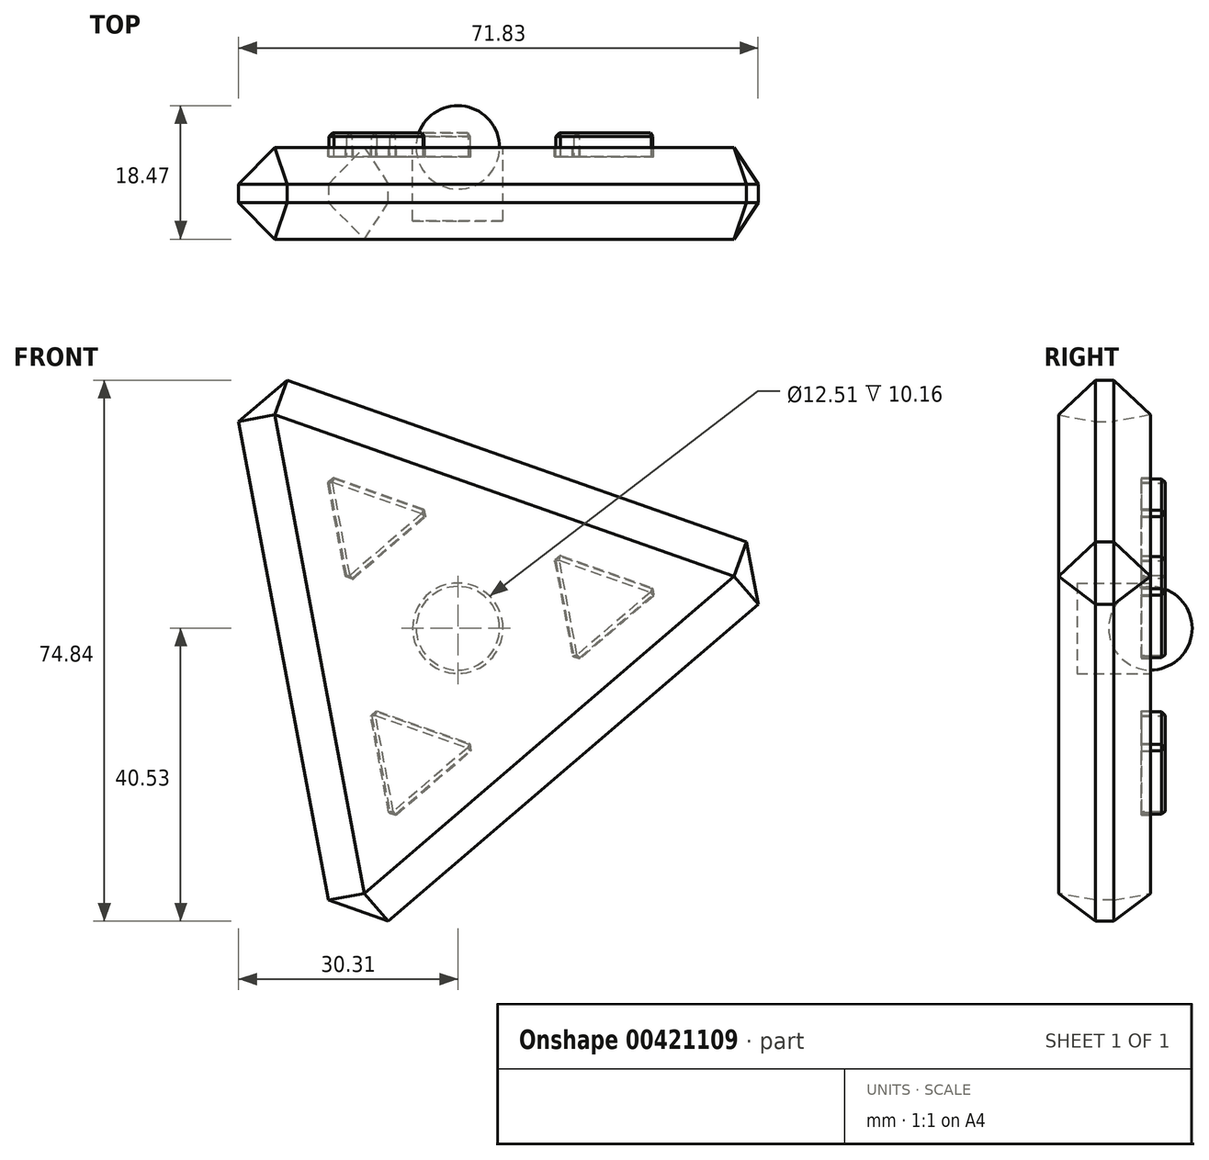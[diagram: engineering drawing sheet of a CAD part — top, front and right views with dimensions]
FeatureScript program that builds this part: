
annotation { "Feature Type Name" : "Feature", "Feature Type Description" : "" }
export const myFeature = defineFeature(function(context is Context, id is Id, definition is map)
    precondition{}
    {
        {
            var Q0;
            Q0=qCreatedBy(makeId("Front.planeOp"),FACE);
            var sketch = newSketch(context, id + "F0", { "sketchPlane" : qUnion([Q0])});
            skCircle(sketch, "E0.cCircle", {"center": v(0, 0) * mm, "radius": 49.04 * mm, "construction": true});
            skLineSegment(sketch, "E0.0", {"start": v(-16.28, -46.26) * mm, "end": v(-31.93, 37.23) * mm});
            skLineSegment(sketch, "E0.1", {"start": v(-31.93, 37.23) * mm, "end": v(48.2, 9.03) * mm});
            skLineSegment(sketch, "E0.2", {"start": v(48.2, 9.03) * mm, "end": v(-16.28, -46.26) * mm});
            skSolve(sketch);
        }
        {
            var Q0;
            Q0=makeQuery(id+"F0.imprint","IMPRINT",FACE,{"disambiguationData":[TD([[makeQuery(id+"F0.imprint","IMPRINT",EDGE,{"derivedFrom":sQuery(id+"F0.wireOp",EDGE,"E0.0")}),-1.0]])]});
            extrude(context, id + "F1", {"entities" : qUnion([Q0]), "depth" : 12.7 * mm});
        }
        {
            var Q0;
            Q0=makeQuery(id+"F1.opExtrude","CAP_FACE",FACE,{"disambiguationData":[OSD([sQuery(id+"F0.wireOp",EDGE,"E0.0"),sQuery(id+"F0.wireOp",EDGE,"E0.1"),sQuery(id+"F0.wireOp",EDGE,"E0.2")])],"isStart":true});
            var Q1;
            Q1=makeQuery(id+"F1.opExtrude","SWEPT_EDGE",EDGE,{"disambiguationData":[OSD([sQuery(id+"F0.wireOp",EDGE,"E0.1"),sQuery(id+"F0.wireOp",EDGE,"E0.2")])]});
            var Q2;
            Q2=makeQuery(id+"F1.opExtrude","SWEPT_EDGE",EDGE,{"disambiguationData":[OSD([sQuery(id+"F0.wireOp",EDGE,"E0.0"),sQuery(id+"F0.wireOp",EDGE,"E0.1")])]});
            var Q3;
            Q3=makeQuery(id+"F1.opExtrude","SWEPT_EDGE",EDGE,{"disambiguationData":[OSD([sQuery(id+"F0.wireOp",EDGE,"E0.0"),sQuery(id+"F0.wireOp",EDGE,"E0.2")])]});
            var Q4;
            Q4=makeQuery(id+"F1.opExtrude","CAP_FACE",FACE,{"disambiguationData":[OSD([sQuery(id+"F0.wireOp",EDGE,"E0.0"),sQuery(id+"F0.wireOp",EDGE,"E0.1"),sQuery(id+"F0.wireOp",EDGE,"E0.2")])],"isStart":false});
            chamfer(context, id + "F2", {"entities" : qUnion([Q0, Q1, Q2, Q3, Q4]), "width" : 5.08 * mm, "tangentPropagation" : true});
        }
        {
            var Q0;
            Q0=makeQuery(id+"F1.opExtrude","CAP_FACE",FACE,{"disambiguationData":[OSD([sQuery(id+"F0.wireOp",EDGE,"E0.0"),sQuery(id+"F0.wireOp",EDGE,"E0.1"),sQuery(id+"F0.wireOp",EDGE,"E0.2")])],"isStart":true});
            var sketch = newSketch(context, id + "F3", { "sketchPlane" : qUnion([Q0])});
            skCircle(sketch, "E1", {"center": v(0, 0) * mm, "radius": 6.26 * mm});
            skSolve(sketch);
        }
        {
            var Q0;
            Q0 = qSketchRegion(id + "F3", true);
            extrude(context, id + "F4", {"entities" : qUnion([Q0]), "operationType" : NewBodyOperationType.REMOVE, "oppositeDirection" : true, "depth" : 10.16 * mm});
        }
        {
            var Q0;
            Q0=makeQuery(id+"F1.opExtrude","CAP_FACE",FACE,{"disambiguationData":[OSD([sQuery(id+"F0.wireOp",EDGE,"E0.0"),sQuery(id+"F0.wireOp",EDGE,"E0.1"),sQuery(id+"F0.wireOp",EDGE,"E0.2")])],"isStart":true});
            var sketch = newSketch(context, id + "F5", { "sketchPlane" : qUnion([Q0])});
            skPoint(sketch, "E2", {"position": v(12.4, 14.46) * mm});
            skPoint(sketch, "E3", {"position": v(6.32, -17.97) * mm});
            skPoint(sketch, "E4", {"position": v(-19.05, 3.57) * mm});
            skCircle(sketch, "E5.cCircle", {"center": v(12.4, 14.46) * mm, "radius": 8.57 * mm, "construction": true});
            skLineSegment(sketch, "E5.0", {"start": v(17.98, 20.97) * mm, "end": v(15.25, 6.37) * mm});
            skLineSegment(sketch, "E5.1", {"start": v(15.25, 6.37) * mm, "end": v(3.98, 16.04) * mm});
            skLineSegment(sketch, "E5.2", {"start": v(3.98, 16.04) * mm, "end": v(17.98, 20.97) * mm});
            skCircle(sketch, "E6.cCircle", {"center": v(6.32, -17.97) * mm, "radius": 8.8 * mm, "construction": true});
            skLineSegment(sketch, "E6.0", {"start": v(9.24, -26.27) * mm, "end": v(-2.33, -16.35) * mm});
            skLineSegment(sketch, "E6.1", {"start": v(-2.33, -16.35) * mm, "end": v(12.05, -11.29) * mm});
            skLineSegment(sketch, "E6.2", {"start": v(12.05, -11.29) * mm, "end": v(9.24, -26.27) * mm});
            skCircle(sketch, "E7.cCircle", {"center": v(-19.05, 3.57) * mm, "radius": 8.7 * mm, "construction": true});
            skLineSegment(sketch, "E7.0", {"start": v(-27.6, 5.17) * mm, "end": v(-13.38, 10.18) * mm});
            skLineSegment(sketch, "E7.1", {"start": v(-13.38, 10.18) * mm, "end": v(-16.16, -4.64) * mm});
            skLineSegment(sketch, "E7.2", {"start": v(-16.16, -4.64) * mm, "end": v(-27.6, 5.17) * mm});
            skSolve(sketch);
        }
        {
            var Q0;
            Q0 = qSketchRegion(id + "F5", true);
            extrude(context, id + "F6", {"entities" : qUnion([Q0]), "operationType" : NewBodyOperationType.ADD, "depth" : 2.03 * mm});
        }
        {
            var Q0;
            Q0=makeQuery(id+"F6.opExtrude","CAP_FACE",FACE,{"disambiguationData":[OSD([sQuery(id+"F5.wireOp",EDGE,"E7.0"),sQuery(id+"F5.wireOp",EDGE,"E7.1"),sQuery(id+"F5.wireOp",EDGE,"E7.2")])],"isStart":false});
            var Q1;
            Q1=makeQuery(id+"F6.opExtrude","CAP_FACE",FACE,{"disambiguationData":[OSD([sQuery(id+"F5.wireOp",EDGE,"E5.0"),sQuery(id+"F5.wireOp",EDGE,"E5.1"),sQuery(id+"F5.wireOp",EDGE,"E5.2")])],"isStart":false});
            var Q2;
            Q2=makeQuery(id+"F6.opExtrude","CAP_FACE",FACE,{"disambiguationData":[OSD([sQuery(id+"F5.wireOp",EDGE,"E6.0"),sQuery(id+"F5.wireOp",EDGE,"E6.1"),sQuery(id+"F5.wireOp",EDGE,"E6.2")])],"isStart":false});
            var Q3;
            Q3=makeQuery(id+"F6.opExtrude","SWEPT_EDGE",EDGE,{"disambiguationData":[OSD([sQuery(id+"F5.wireOp",EDGE,"E7.1"),sQuery(id+"F5.wireOp",EDGE,"E7.2")])]});
            var Q4;
            Q4=makeQuery(id+"F6.opExtrude","SWEPT_EDGE",EDGE,{"disambiguationData":[OSD([sQuery(id+"F5.wireOp",EDGE,"E7.0"),sQuery(id+"F5.wireOp",EDGE,"E7.2")])]});
            var Q5;
            Q5=makeQuery(id+"F6.opExtrude","SWEPT_EDGE",EDGE,{"disambiguationData":[OSD([sQuery(id+"F5.wireOp",EDGE,"E7.0"),sQuery(id+"F5.wireOp",EDGE,"E7.1")])]});
            var Q6;
            Q6=makeQuery(id+"F6.opExtrude","SWEPT_EDGE",EDGE,{"disambiguationData":[OSD([sQuery(id+"F5.wireOp",EDGE,"E5.1"),sQuery(id+"F5.wireOp",EDGE,"E5.2")])]});
            var Q7;
            Q7=makeQuery(id+"F6.opExtrude","SWEPT_EDGE",EDGE,{"disambiguationData":[OSD([sQuery(id+"F5.wireOp",EDGE,"E5.0"),sQuery(id+"F5.wireOp",EDGE,"E5.2")])]});
            var Q8;
            Q8=makeQuery(id+"F6.opExtrude","SWEPT_EDGE",EDGE,{"disambiguationData":[OSD([sQuery(id+"F5.wireOp",EDGE,"E5.0"),sQuery(id+"F5.wireOp",EDGE,"E5.1")])]});
            var Q9;
            Q9=makeQuery(id+"F6.opExtrude","SWEPT_EDGE",EDGE,{"disambiguationData":[OSD([sQuery(id+"F5.wireOp",EDGE,"E6.0"),sQuery(id+"F5.wireOp",EDGE,"E6.2")])]});
            var Q10;
            Q10=makeQuery(id+"F6.opExtrude","SWEPT_EDGE",EDGE,{"disambiguationData":[OSD([sQuery(id+"F5.wireOp",EDGE,"E6.1"),sQuery(id+"F5.wireOp",EDGE,"E6.2")])]});
            var Q11;
            Q11=makeQuery(id+"F6.opExtrude","SWEPT_EDGE",EDGE,{"disambiguationData":[OSD([sQuery(id+"F5.wireOp",EDGE,"E6.0"),sQuery(id+"F5.wireOp",EDGE,"E6.1")])]});
            chamfer(context, id + "F7", {"entities" : qUnion([Q0, Q1, Q2, Q3, Q4, Q5, Q6, Q7, Q8, Q9, Q10, Q11]), "width" : 0.5 * mm, "tangentPropagation" : true});
        }
        {
            var Q0;
            Q0=makeQuery(id+"F1.opExtrude","CAP_FACE",FACE,{"disambiguationData":[OSD([sQuery(id+"F0.wireOp",EDGE,"E0.0"),sQuery(id+"F0.wireOp",EDGE,"E0.1"),sQuery(id+"F0.wireOp",EDGE,"E0.2")])],"isStart":true});
            var sketch = newSketch(context, id + "F8", { "sketchPlane" : qUnion([Q0])});
            skLineSegment(sketch, "E8", {"start": v(4.65, 16.36) * mm, "end": v(4.5, 15.5) * mm});
            skLineSegment(sketch, "E9", {"start": v(4.5, 15.5) * mm, "end": v(4.5, 15.4) * mm});
            skLineSegment(sketch, "E10", {"start": v(14.58, 6.8) * mm, "end": v(15.46, 7.1) * mm});
            skLineSegment(sketch, "E11", {"start": v(14.58, 6.8) * mm, "end": v(14.48, 6.83) * mm});
            skLineSegment(sketch, "E12", {"start": v(14.48, 6.83) * mm, "end": v(4.5, 15.4) * mm});
            skLineSegment(sketch, "E13", {"start": v(17.15, 20.82) * mm, "end": v(17.96, 20.17) * mm});
            skLineSegment(sketch, "E14", {"start": v(17.15, 20.82) * mm, "end": v(17.09, 20.82) * mm});
            skLineSegment(sketch, "E15", {"start": v(17.09, 20.82) * mm, "end": v(4.8, 16.5) * mm});
            skLineSegment(sketch, "E16", {"start": v(4.65, 16.36) * mm, "end": v(4.8, 16.5) * mm});
            skLineSegment(sketch, "E17", {"start": v(17.96, 20.1) * mm, "end": v(17.96, 20.17) * mm});
            skLineSegment(sketch, "E18", {"start": v(15.55, 7.21) * mm, "end": v(15.46, 7.1) * mm});
            skLineSegment(sketch, "E19", {"start": v(15.55, 7.21) * mm, "end": v(17.96, 20.1) * mm});
            skLineSegment(sketch, "E20", {"start": v(4.8, 16.33) * mm, "end": v(4.64, 15.47) * mm});
            skLineSegment(sketch, "E21", {"start": v(4.64, 15.47) * mm, "end": v(14.58, 6.95) * mm});
            skLineSegment(sketch, "E22", {"start": v(14.58, 6.95) * mm, "end": v(15.4, 7.24) * mm});
            skLineSegment(sketch, "E23", {"start": v(15.4, 7.24) * mm, "end": v(17.82, 20.1) * mm});
            skLineSegment(sketch, "E24", {"start": v(17.82, 20.1) * mm, "end": v(17.15, 20.68) * mm});
            skLineSegment(sketch, "E25", {"start": v(17.15, 20.68) * mm, "end": v(4.8, 16.33) * mm});
            skSolve(sketch);
        }
        {
            var Q0;
            Q0 = qSketchRegion(id + "F8", true);
            extrude(context, id + "F9", {"entities" : qUnion([Q0]), "operationType" : NewBodyOperationType.REMOVE, "oppositeDirection" : true, "depth" : 1.27 * mm});
        }
        {
            var Q0;
            Q0=makeQuery(id+"F1.opExtrude","CAP_FACE",FACE,{"disambiguationData":[OSD([sQuery(id+"F0.wireOp",EDGE,"E0.0"),sQuery(id+"F0.wireOp",EDGE,"E0.1"),sQuery(id+"F0.wireOp",EDGE,"E0.2")])],"isStart":true});
            var sketch = newSketch(context, id + "F10", { "sketchPlane" : qUnion([Q0])});
            skLineSegment(sketch, "E26", {"start": v(-1.66, -16.03) * mm, "end": v(-1.8, -16.92) * mm});
            skLineSegment(sketch, "E27", {"start": v(-1.66, -16.03) * mm, "end": v(-1.55, -15.9) * mm});
            skLineSegment(sketch, "E28", {"start": v(-1.76, -17.03) * mm, "end": v(-1.8, -16.92) * mm});
            skLineSegment(sketch, "E29", {"start": v(12.04, -12.18) * mm, "end": v(12, -12.04) * mm});
            skLineSegment(sketch, "E30", {"start": v(11.32, -11.47) * mm, "end": v(11.22, -11.44) * mm});
            skLineSegment(sketch, "E31", {"start": v(11.32, -11.47) * mm, "end": v(12, -12.04) * mm});
            skLineSegment(sketch, "E32", {"start": v(11.22, -11.44) * mm, "end": v(-1.55, -15.9) * mm});
            skLineSegment(sketch, "E33", {"start": v(8.49, -25.8) * mm, "end": v(8.58, -25.86) * mm});
            skLineSegment(sketch, "E34", {"start": v(9.56, -25.44) * mm, "end": v(9.46, -25.56) * mm});
            skLineSegment(sketch, "E35", {"start": v(9.46, -25.56) * mm, "end": v(8.58, -25.86) * mm});
            skLineSegment(sketch, "E36", {"start": v(8.49, -25.8) * mm, "end": v(-1.76, -17.03) * mm});
            skLineSegment(sketch, "E37", {"start": v(9.56, -25.44) * mm, "end": v(12.04, -12.18) * mm});
            skLineSegment(sketch, "E38", {"start": v(11.22, -11.58) * mm, "end": v(11.9, -12.15) * mm});
            skLineSegment(sketch, "E39", {"start": v(11.9, -12.15) * mm, "end": v(9.4, -25.4) * mm});
            skLineSegment(sketch, "E40", {"start": v(9.4, -25.4) * mm, "end": v(8.58, -25.7) * mm});
            skLineSegment(sketch, "E41", {"start": v(8.58, -25.7) * mm, "end": v(-1.66, -16.92) * mm});
            skLineSegment(sketch, "E42", {"start": v(-1.66, -16.92) * mm, "end": v(-1.5, -16.06) * mm});
            skLineSegment(sketch, "E43", {"start": v(-1.5, -16.06) * mm, "end": v(11.22, -11.58) * mm});
            skSolve(sketch);
        }
        {
            var Q0;
            Q0 = qSketchRegion(id + "F10", true);
            extrude(context, id + "F11", {"entities" : qUnion([Q0]), "operationType" : NewBodyOperationType.REMOVE, "oppositeDirection" : true, "depth" : 1.27 * mm});
        }
        {
            var Q0;
            Q0=makeQuery(id+"F1.opExtrude","CAP_FACE",FACE,{"disambiguationData":[OSD([sQuery(id+"F0.wireOp",EDGE,"E0.0"),sQuery(id+"F0.wireOp",EDGE,"E0.1"),sQuery(id+"F0.wireOp",EDGE,"E0.2")])],"isStart":true});
            var sketch = newSketch(context, id + "F12", { "sketchPlane" : qUnion([Q0])});
            skLineSegment(sketch, "E44", {"start": v(-16.92, -4.18) * mm, "end": v(-16.78, -4.2) * mm});
            skLineSegment(sketch, "E45", {"start": v(-15.85, -3.8) * mm, "end": v(-15.95, -3.92) * mm});
            skLineSegment(sketch, "E46", {"start": v(-15.95, -3.92) * mm, "end": v(-16.78, -4.2) * mm});
            skLineSegment(sketch, "E47", {"start": v(-13.39, 9.28) * mm, "end": v(-13.45, 9.43) * mm});
            skLineSegment(sketch, "E48", {"start": v(-14.27, 10.04) * mm, "end": v(-14.18, 10.04) * mm});
            skLineSegment(sketch, "E49", {"start": v(-14.18, 10.04) * mm, "end": v(-13.45, 9.43) * mm});
            skLineSegment(sketch, "E50", {"start": v(-13.39, 9.28) * mm, "end": v(-15.85, -3.8) * mm});
            skLineSegment(sketch, "E51", {"start": v(-26.83, 5.61) * mm, "end": v(-26.93, 5.5) * mm});
            skLineSegment(sketch, "E52", {"start": v(-27.04, 4.48) * mm, "end": v(-27.09, 4.63) * mm});
            skLineSegment(sketch, "E53", {"start": v(-26.93, 5.5) * mm, "end": v(-27.09, 4.63) * mm});
            skLineSegment(sketch, "E54", {"start": v(-27.04, 4.48) * mm, "end": v(-16.92, -4.18) * mm});
            skLineSegment(sketch, "E55", {"start": v(-14.27, 10.04) * mm, "end": v(-26.83, 5.61) * mm});
            skLineSegment(sketch, "E56", {"start": v(-26.94, 4.6) * mm, "end": v(-26.78, 5.47) * mm});
            skLineSegment(sketch, "E57", {"start": v(-26.78, 5.47) * mm, "end": v(-14.21, 9.89) * mm});
            skLineSegment(sketch, "E58", {"start": v(-14.21, 9.89) * mm, "end": v(-13.55, 9.31) * mm});
            skLineSegment(sketch, "E59", {"start": v(-13.55, 9.31) * mm, "end": v(-16, -3.78) * mm});
            skLineSegment(sketch, "E60", {"start": v(-16, -3.78) * mm, "end": v(-16.83, -4.07) * mm});
            skLineSegment(sketch, "E61", {"start": v(-16.83, -4.07) * mm, "end": v(-26.94, 4.6) * mm});
            skSolve(sketch);
        }
        {
            var Q0;
            Q0 = qSketchRegion(id + "F12", true);
            extrude(context, id + "F13", {"entities" : qUnion([Q0]), "operationType" : NewBodyOperationType.REMOVE, "oppositeDirection" : true, "depth" : 1.27 * mm});
        }
        {
            var Q0;
            Q0=makeQuery(id+"F1.opExtrude","CAP_FACE",FACE,{"disambiguationData":[OSD([sQuery(id+"F0.wireOp",EDGE,"E0.0"),sQuery(id+"F0.wireOp",EDGE,"E0.1"),sQuery(id+"F0.wireOp",EDGE,"E0.2")])],"isStart":true});
            var sketch = newSketch(context, id + "F14", { "sketchPlane" : qUnion([Q0])});
            skCircle(sketch, "E62", {"center": v(0, 0) * mm, "radius": 5.77 * mm});
            skLineSegment(sketch, "E63", {"start": v(0, 5.77) * mm, "end": v(0, -5.77) * mm});
            skSolve(sketch);
        }
        {
            var Q0;
            {var subQ0=sQuery(id+"F14.wireOp",EDGE,"E63");Q0=makeQuery(id+"F14.imprint","IMPRINT",FACE,{"disambiguationData":[TD([[makeQuery(id+"F14.imprint","IMPRINT",EDGE,{"derivedFrom":subQ0}),-1.0]])]});}
            var Q1;
            Q1=sQuery(id+"F14.wireOp",EDGE,"E63");
            revolve(context, id + "F15", {"entities" : qUnion([Q0]), "axis" : qUnion([Q1]), "revolveType" : RevolveType.FULL});
        }
    });
